# Revit family: RN 91060 Optifitt-Serra-Verlängerung
name_source: partatom
category: Rohrformteile
units: mm (PartAtom-declared; Revit-internal decimal feet)

## family parameters
Arbeitsebenenbasiert = Nein
Beim Laden mit Abzugskörper schneiden = Nein
Bemaßung runder Anschluss = Durchmesser verwenden
Gemeinsam genutzt = Nein
Immer vertikal = Ja
Teiletyp = Nicht definiert

## types (13) — shared parameters
1.010.00.2 Blattnummer der Richtlinie = 29
1.010.00.3 Ausgabedatum (Monat) der Richtlinie = 201308
1.010.00.4 Herstellername = R. Nussbaum AG
1.010.00.5 Revisionsdatum der Datei = 20190521
1.010.00.6 Webadresse des Herstellers = http://www.nussbaum.ch
1.100.00.4 Produktbezeichnung = Versorgung
1.110.00.2 Index = 3
1.110.00.4 Produktbezeichnung = Optifitt-Serra
1.960/3L.00.8 Link (URL) = https://www.nussbaum.ch
29.700.00.4 Produktname = Optifitt-Serra-Verlängerung
29.700.00.5 Produktkennung = 2
29.700.00.6 Querschnittsform = 1
29.700.00.7 Nennweitensystem = DN
29.700.00.8 Nenndrucksystem = PN
29.710.02.4 Nenndruck = 16
29.710.02.5 max. zul. Überdruck [hPa] = 1600
29.710.02.7 max. zul. Dauer-Betriebsdruck [hPa] = 1600
29.710.02.9 max. zul. Dauer-Betriebstemperatur [°C] = 90
Connector Visibility = Nein
EnclosingSpace Visibility = Nein
R. Nussbaum AG 91060.51 de Visibility = Nein
R. Nussbaum AG 91060.52 de Visibility = Nein
R. Nussbaum AG 91060.68 de Visibility = Nein
R. Nussbaum AG 91060.69 de Visibility = Nein
R. Nussbaum AG 91060.71 de Visibility = Nein
R. Nussbaum AG 91060.72 de Visibility = Nein
R. Nussbaum AG 91060.74 de Visibility = Nein

## per-type parameters (varying)
- DN=2: 1.800.00.3 TGA-Nummer=01900300000000000000000000000000000000000000000020000000000000000049; 1.800.00.4 Kommentarfeld=91060.70, Optifitt-Serra-Verlängerung, DN=15, L=100; 1.810.00.3 Hersteller-Bestellnummer=91060.7; 1.810.00.4 DATANORM-Nummer=91060.7; 1.810.00.6 GTIN-Nummer=7612945036476; 29.710.02.10 Formstück-Gewicht [kg]=0.271; 29.710.02.3 Benennung=Optifitt-Serra-Verlängerung, DN=15, L=100; CONNECTOR0_DIAMETER_dX_0r=15 mm; CONNECTOR0_dX_01=11 mm; CONNECTOR0_ref_dX=11 mm; CONNECTOR1_DIAMETER_dX_0r=15 mm; CONNECTOR1_dX_00=98 mm; CONNECTOR1_dX_01=111 mm; CONNECTOR1_ref_dX=98 mm; Hersteller=R. Nussbaum AG; Modell=91060.7; R. Nussbaum AG 91060.53 de Visibility=Nein; R. Nussbaum AG 91060.54 de Visibility=Nein; R. Nussbaum AG 91060.55 de Visibility=Nein; R. Nussbaum AG 91060.56 de Visibility=Nein; R. Nussbaum AG 91060.62 de Visibility=Nein; R. Nussbaum AG 91060.63 de Visibility=Nein; R. Nussbaum AG 91060.64 de Visibility=Nein; R. Nussbaum AG 91060.65 de Visibility=Nein; R. Nussbaum AG 91060.66 de Visibility=Nein; R. Nussbaum AG 91060.67 de Visibility=Nein; R. Nussbaum AG 91060.70 de Visibility=Ja; R. Nussbaum AG 91060.73 de Visibility=Nein; R. Nussbaum AG 91060.75 de Visibility=Nein; Typenkommentare=Optifitt-Serra-Verlängerung  DN=15; URL=https://www.nussbaum.ch
- DN=1: 1.800.00.3 TGA-Nummer=01900300000000000000000000000000000000000000000020000000000000000045; 1.800.00.4 Kommentarfeld=91060.75, Optifitt-Serra-Verlängerung, DN=20, L=40; 1.810.00.3 Hersteller-Bestellnummer=91060.75; 1.810.00.4 DATANORM-Nummer=91060.75; 1.810.00.5 StLB-Nummer=214.413; 1.810.00.6 GTIN-Nummer=7612945036520; 29.710.02.10 Formstück-Gewicht [kg]=0.125; 29.710.02.3 Benennung=Optifitt-Serra-Verlängerung, DN=20, L=40; CONNECTOR0_DIAMETER_dX_0r=20 mm; CONNECTOR0_dX_01=12 mm  [stored 0.0393701 ft]; CONNECTOR0_ref_dX=12 mm  [stored 0.0393701 ft]; CONNECTOR1_DIAMETER_dX_0r=20 mm; CONNECTOR1_dX_00=37 mm; CONNECTOR1_dX_01=52 mm; CONNECTOR1_ref_dX=37 mm; Hersteller=R. Nussbaum AG; Modell=91060.75; R. Nussbaum AG 91060.53 de Visibility=Nein; R. Nussbaum AG 91060.54 de Visibility=Nein; R. Nussbaum AG 91060.55 de Visibility=Nein; R. Nussbaum AG 91060.56 de Visibility=Nein; R. Nussbaum AG 91060.62 de Visibility=Nein; R. Nussbaum AG 91060.63 de Visibility=Nein; R. Nussbaum AG 91060.64 de Visibility=Nein; R. Nussbaum AG 91060.65 de Visibility=Nein; R. Nussbaum AG 91060.66 de Visibility=Nein; R. Nussbaum AG 91060.67 de Visibility=Nein; R. Nussbaum AG 91060.70 de Visibility=Nein; R. Nussbaum AG 91060.73 de Visibility=Nein; R. Nussbaum AG 91060.75 de Visibility=Ja; Typenkommentare=Optifitt-Serra-Verlängerung  DN=20; URL=https://www.nussbaum.ch
- DN=20: 1.800.00.3 TGA-Nummer=01900300000000000000000000000000000000000000000020000000000000000043; 1.800.00.4 Kommentarfeld=91060.73, Optifitt-Serra-Verlängerung, DN=20, L=25; 1.810.00.3 Hersteller-Bestellnummer=91060.73; 1.810.00.4 DATANORM-Nummer=91060.73; 1.810.00.6 GTIN-Nummer=7612945036506; 29.710.02.10 Formstück-Gewicht [kg]=0.094; 29.710.02.3 Benennung=Optifitt-Serra-Verlängerung, DN=20, L=25; CONNECTOR0_DIAMETER_dX_0r=20 mm; CONNECTOR0_dX_01=12 mm  [stored 0.0393701 ft]; CONNECTOR0_ref_dX=12 mm  [stored 0.0393701 ft]; CONNECTOR1_DIAMETER_dX_0r=20 mm; CONNECTOR1_dX_00=22 mm; CONNECTOR1_dX_01=37 mm; CONNECTOR1_ref_dX=22 mm; R. Nussbaum AG 91060.53 de Visibility=Nein; R. Nussbaum AG 91060.54 de Visibility=Nein; R. Nussbaum AG 91060.55 de Visibility=Nein; R. Nussbaum AG 91060.56 de Visibility=Nein; R. Nussbaum AG 91060.62 de Visibility=Nein; R. Nussbaum AG 91060.63 de Visibility=Nein; R. Nussbaum AG 91060.64 de Visibility=Nein; R. Nussbaum AG 91060.65 de Visibility=Nein; R. Nussbaum AG 91060.66 de Visibility=Nein; R. Nussbaum AG 91060.67 de Visibility=Nein; R. Nussbaum AG 91060.70 de Visibility=Nein; R. Nussbaum AG 91060.73 de Visibility=Ja; R. Nussbaum AG 91060.75 de Visibility=Nein
- DN=15: 1.800.00.3 TGA-Nummer=01900300000000000000000000000000000000000000000020000000000000000038; 1.800.00.4 Kommentarfeld=91060.67, Optifitt-Serra-Verlängerung, DN=15, L=50; 1.810.00.3 Hersteller-Bestellnummer=91060.67; 1.810.00.4 DATANORM-Nummer=91060.67; 1.810.00.6 GTIN-Nummer=7612945036445; 29.710.02.10 Formstück-Gewicht [kg]=0.135; 29.710.02.3 Benennung=Optifitt-Serra-Verlängerung, DN=15, L=50; CONNECTOR0_DIAMETER_dX_0r=15 mm; CONNECTOR0_dX_01=11 mm; CONNECTOR0_ref_dX=11 mm; CONNECTOR1_DIAMETER_dX_0r=15 mm; CONNECTOR1_dX_00=48 mm; CONNECTOR1_dX_01=61 mm; CONNECTOR1_ref_dX=48 mm; R. Nussbaum AG 91060.53 de Visibility=Nein; R. Nussbaum AG 91060.54 de Visibility=Nein; R. Nussbaum AG 91060.55 de Visibility=Nein; R. Nussbaum AG 91060.56 de Visibility=Nein; R. Nussbaum AG 91060.62 de Visibility=Nein; R. Nussbaum AG 91060.63 de Visibility=Nein; R. Nussbaum AG 91060.64 de Visibility=Nein; R. Nussbaum AG 91060.65 de Visibility=Nein; R. Nussbaum AG 91060.66 de Visibility=Nein; R. Nussbaum AG 91060.67 de Visibility=Ja; R. Nussbaum AG 91060.70 de Visibility=Nein; R. Nussbaum AG 91060.73 de Visibility=Nein; R. Nussbaum AG 91060.75 de Visibility=Nein
- DN=11: 1.800.00.3 TGA-Nummer=01900300000000000000000000000000000000000000000020000000000000000037; 1.800.00.4 Kommentarfeld=91060.66, Optifitt-Serra-Verlängerung, DN=15, L=40; 1.810.00.3 Hersteller-Bestellnummer=91060.66; 1.810.00.4 DATANORM-Nummer=91060.66; 1.810.00.5 StLB-Nummer=214.412; 1.810.00.6 GTIN-Nummer=7612945036438; 29.710.02.10 Formstück-Gewicht [kg]=0.107; 29.710.02.3 Benennung=Optifitt-Serra-Verlängerung, DN=15, L=40; CONNECTOR0_DIAMETER_dX_0r=15 mm; CONNECTOR0_dX_01=11 mm; CONNECTOR0_ref_dX=11 mm; CONNECTOR1_DIAMETER_dX_0r=15 mm; CONNECTOR1_dX_00=38 mm; CONNECTOR1_dX_01=51 mm; CONNECTOR1_ref_dX=38 mm; Hersteller=R. Nussbaum AG; Modell=91060.66; R. Nussbaum AG 91060.53 de Visibility=Nein; R. Nussbaum AG 91060.54 de Visibility=Nein; R. Nussbaum AG 91060.55 de Visibility=Nein; R. Nussbaum AG 91060.56 de Visibility=Nein; R. Nussbaum AG 91060.62 de Visibility=Nein; R. Nussbaum AG 91060.63 de Visibility=Nein; R. Nussbaum AG 91060.64 de Visibility=Nein; R. Nussbaum AG 91060.65 de Visibility=Nein; R. Nussbaum AG 91060.66 de Visibility=Ja; R. Nussbaum AG 91060.67 de Visibility=Nein; R. Nussbaum AG 91060.70 de Visibility=Nein; R. Nussbaum AG 91060.73 de Visibility=Nein; R. Nussbaum AG 91060.75 de Visibility=Nein; Typenkommentare=Optifitt-Serra-Verlängerung  DN=15; URL=https://www.nussbaum.ch
- DN=9: 1.800.00.3 TGA-Nummer=01900300000000000000000000000000000000000000000020000000000000000036; 1.800.00.4 Kommentarfeld=91060.65, Optifitt-Serra-Verlängerung, DN=15, L=30; 1.810.00.3 Hersteller-Bestellnummer=91060.65; 1.810.00.4 DATANORM-Nummer=91060.65; 1.810.00.6 GTIN-Nummer=7612945036421; 29.710.02.10 Formstück-Gewicht [kg]=0.088; 29.710.02.3 Benennung=Optifitt-Serra-Verlängerung, DN=15, L=30; CONNECTOR0_DIAMETER_dX_0r=15 mm; CONNECTOR0_dX_01=11 mm; CONNECTOR0_ref_dX=11 mm; CONNECTOR1_DIAMETER_dX_0r=15 mm; CONNECTOR1_dX_00=28 mm; CONNECTOR1_dX_01=41 mm; CONNECTOR1_ref_dX=28 mm; Hersteller=R. Nussbaum AG; Modell=91060.65; R. Nussbaum AG 91060.53 de Visibility=Nein; R. Nussbaum AG 91060.54 de Visibility=Nein; R. Nussbaum AG 91060.55 de Visibility=Nein; R. Nussbaum AG 91060.56 de Visibility=Nein; R. Nussbaum AG 91060.62 de Visibility=Nein; R. Nussbaum AG 91060.63 de Visibility=Nein; R. Nussbaum AG 91060.64 de Visibility=Nein; R. Nussbaum AG 91060.65 de Visibility=Ja; R. Nussbaum AG 91060.66 de Visibility=Nein; R. Nussbaum AG 91060.67 de Visibility=Nein; R. Nussbaum AG 91060.70 de Visibility=Nein; R. Nussbaum AG 91060.73 de Visibility=Nein; R. Nussbaum AG 91060.75 de Visibility=Nein; Typenkommentare=Optifitt-Serra-Verlängerung  DN=15; URL=https://www.nussbaum.ch
- DN=8: 1.800.00.3 TGA-Nummer=01900300000000000000000000000000000000000000000020000000000000000035; 1.800.00.4 Kommentarfeld=91060.64, Optifitt-Serra-Verlängerung, DN=15, L=25; 1.810.00.3 Hersteller-Bestellnummer=91060.64; 1.810.00.4 DATANORM-Nummer=91060.64; 1.810.00.6 GTIN-Nummer=7612945036414; 29.710.02.10 Formstück-Gewicht [kg]=0.075; 29.710.02.3 Benennung=Optifitt-Serra-Verlängerung, DN=15, L=25; CONNECTOR0_DIAMETER_dX_0r=15 mm; CONNECTOR0_dX_01=11 mm; CONNECTOR0_ref_dX=11 mm; CONNECTOR1_DIAMETER_dX_0r=15 mm; CONNECTOR1_dX_00=23 mm; CONNECTOR1_dX_01=36 mm; CONNECTOR1_ref_dX=23 mm; Hersteller=R. Nussbaum AG; Modell=91060.64; R. Nussbaum AG 91060.53 de Visibility=Nein; R. Nussbaum AG 91060.54 de Visibility=Nein; R. Nussbaum AG 91060.55 de Visibility=Nein; R. Nussbaum AG 91060.56 de Visibility=Nein; R. Nussbaum AG 91060.62 de Visibility=Nein; R. Nussbaum AG 91060.63 de Visibility=Nein; R. Nussbaum AG 91060.64 de Visibility=Ja; R. Nussbaum AG 91060.65 de Visibility=Nein; R. Nussbaum AG 91060.66 de Visibility=Nein; R. Nussbaum AG 91060.67 de Visibility=Nein; R. Nussbaum AG 91060.70 de Visibility=Nein; R. Nussbaum AG 91060.73 de Visibility=Nein; R. Nussbaum AG 91060.75 de Visibility=Nein; Typenkommentare=Optifitt-Serra-Verlängerung  DN=15; URL=https://www.nussbaum.ch
- DN=7: 1.800.00.3 TGA-Nummer=01900300000000000000000000000000000000000000000020000000000000000034; 1.800.00.4 Kommentarfeld=91060.63, Optifitt-Serra-Verlängerung, DN=15, L=20; 1.810.00.3 Hersteller-Bestellnummer=91060.63; 1.810.00.4 DATANORM-Nummer=91060.63; 1.810.00.6 GTIN-Nummer=7612945036407; 29.710.02.10 Formstück-Gewicht [kg]=0.067; 29.710.02.3 Benennung=Optifitt-Serra-Verlängerung, DN=15, L=20; CONNECTOR0_DIAMETER_dX_0r=15 mm; CONNECTOR0_dX_01=11 mm; CONNECTOR0_ref_dX=11 mm; CONNECTOR1_DIAMETER_dX_0r=15 mm; CONNECTOR1_dX_00=18 mm; CONNECTOR1_dX_01=31 mm; CONNECTOR1_ref_dX=18 mm; Hersteller=R. Nussbaum AG; Modell=91060.63; R. Nussbaum AG 91060.53 de Visibility=Nein; R. Nussbaum AG 91060.54 de Visibility=Nein; R. Nussbaum AG 91060.55 de Visibility=Nein; R. Nussbaum AG 91060.56 de Visibility=Nein; R. Nussbaum AG 91060.62 de Visibility=Nein; R. Nussbaum AG 91060.63 de Visibility=Ja; R. Nussbaum AG 91060.64 de Visibility=Nein; R. Nussbaum AG 91060.65 de Visibility=Nein; R. Nussbaum AG 91060.66 de Visibility=Nein; R. Nussbaum AG 91060.67 de Visibility=Nein; R. Nussbaum AG 91060.70 de Visibility=Nein; R. Nussbaum AG 91060.73 de Visibility=Nein; R. Nussbaum AG 91060.75 de Visibility=Nein; Typenkommentare=Optifitt-Serra-Verlängerung  DN=15; URL=https://www.nussbaum.ch
- DN=3: 1.800.00.3 TGA-Nummer=01900300000000000000000000000000000000000000000020000000000000000033; 1.800.00.4 Kommentarfeld=91060.62, Optifitt-Serra-Verlängerung, DN=15, L=15; 1.810.00.3 Hersteller-Bestellnummer=91060.62; 1.810.00.4 DATANORM-Nummer=91060.62; 1.810.00.6 GTIN-Nummer=7612945036391; 29.710.02.10 Formstück-Gewicht [kg]=0.05; 29.710.02.3 Benennung=Optifitt-Serra-Verlängerung, DN=15, L=15; CONNECTOR0_DIAMETER_dX_0r=15 mm; CONNECTOR0_dX_01=11 mm; CONNECTOR0_ref_dX=11 mm; CONNECTOR1_DIAMETER_dX_0r=15 mm; CONNECTOR1_dX_00=13 mm; CONNECTOR1_dX_01=26 mm; CONNECTOR1_ref_dX=13 mm; Hersteller=R. Nussbaum AG; Modell=91060.62; R. Nussbaum AG 91060.53 de Visibility=Nein; R. Nussbaum AG 91060.54 de Visibility=Nein; R. Nussbaum AG 91060.55 de Visibility=Nein; R. Nussbaum AG 91060.56 de Visibility=Nein; R. Nussbaum AG 91060.62 de Visibility=Ja; R. Nussbaum AG 91060.63 de Visibility=Nein; R. Nussbaum AG 91060.64 de Visibility=Nein; R. Nussbaum AG 91060.65 de Visibility=Nein; R. Nussbaum AG 91060.66 de Visibility=Nein; R. Nussbaum AG 91060.67 de Visibility=Nein; R. Nussbaum AG 91060.70 de Visibility=Nein; R. Nussbaum AG 91060.73 de Visibility=Nein; R. Nussbaum AG 91060.75 de Visibility=Nein; Typenkommentare=Optifitt-Serra-Verlängerung  DN=15; URL=https://www.nussbaum.ch
- DN=10: 1.800.00.3 TGA-Nummer=01900300000000000000000000000000000000000000000020000000000000000032; 1.800.00.4 Kommentarfeld=91060.56, Optifitt-Serra-Verlängerung, DN=10, L=40; 1.810.00.3 Hersteller-Bestellnummer=91060.56; 1.810.00.4 DATANORM-Nummer=91060.56; 1.810.00.5 StLB-Nummer=214.411; 1.810.00.6 GTIN-Nummer=7612945036384; 29.710.02.10 Formstück-Gewicht [kg]=0.075; 29.710.02.3 Benennung=Optifitt-Serra-Verlängerung, DN=10, L=40; CONNECTOR0_DIAMETER_dX_0r=10 mm  [stored 0.0328084 ft]; CONNECTOR0_dX_01=10 mm  [stored 0.0328084 ft]; CONNECTOR0_ref_dX=10 mm  [stored 0.0328084 ft]; CONNECTOR1_DIAMETER_dX_0r=10 mm  [stored 0.0328084 ft]; CONNECTOR1_dX_00=40 mm; CONNECTOR1_dX_01=50 mm; CONNECTOR1_ref_dX=40 mm; Hersteller=R. Nussbaum AG; Modell=91060.56; R. Nussbaum AG 91060.53 de Visibility=Nein; R. Nussbaum AG 91060.54 de Visibility=Nein; R. Nussbaum AG 91060.55 de Visibility=Nein; R. Nussbaum AG 91060.56 de Visibility=Ja; R. Nussbaum AG 91060.62 de Visibility=Nein; R. Nussbaum AG 91060.63 de Visibility=Nein; R. Nussbaum AG 91060.64 de Visibility=Nein; R. Nussbaum AG 91060.65 de Visibility=Nein; R. Nussbaum AG 91060.66 de Visibility=Nein; R. Nussbaum AG 91060.67 de Visibility=Nein; R. Nussbaum AG 91060.70 de Visibility=Nein; R. Nussbaum AG 91060.73 de Visibility=Nein; R. Nussbaum AG 91060.75 de Visibility=Nein; Typenkommentare=Optifitt-Serra-Verlängerung  DN=10; URL=https://www.nussbaum.ch
- DN=6: 1.800.00.3 TGA-Nummer=01900300000000000000000000000000000000000000000020000000000000000031; 1.800.00.4 Kommentarfeld=91060.55, Optifitt-Serra-Verlängerung, DN=10, L=30; 1.810.00.3 Hersteller-Bestellnummer=91060.55; 1.810.00.4 DATANORM-Nummer=91060.55; 1.810.00.6 GTIN-Nummer=7612945036377; 29.710.02.10 Formstück-Gewicht [kg]=0.06; 29.710.02.3 Benennung=Optifitt-Serra-Verlängerung, DN=10, L=30; CONNECTOR0_DIAMETER_dX_0r=10 mm  [stored 0.0328084 ft]; CONNECTOR0_dX_01=10 mm  [stored 0.0328084 ft]; CONNECTOR0_ref_dX=10 mm  [stored 0.0328084 ft]; CONNECTOR1_DIAMETER_dX_0r=10 mm  [stored 0.0328084 ft]; CONNECTOR1_dX_00=30 mm; CONNECTOR1_dX_01=40 mm; CONNECTOR1_ref_dX=30 mm; Hersteller=R. Nussbaum AG; Modell=91060.55; R. Nussbaum AG 91060.53 de Visibility=Nein; R. Nussbaum AG 91060.54 de Visibility=Nein; R. Nussbaum AG 91060.55 de Visibility=Ja; R. Nussbaum AG 91060.56 de Visibility=Nein; R. Nussbaum AG 91060.62 de Visibility=Nein; R. Nussbaum AG 91060.63 de Visibility=Nein; R. Nussbaum AG 91060.64 de Visibility=Nein; R. Nussbaum AG 91060.65 de Visibility=Nein; R. Nussbaum AG 91060.66 de Visibility=Nein; R. Nussbaum AG 91060.67 de Visibility=Nein; R. Nussbaum AG 91060.70 de Visibility=Nein; R. Nussbaum AG 91060.73 de Visibility=Nein; R. Nussbaum AG 91060.75 de Visibility=Nein; Typenkommentare=Optifitt-Serra-Verlängerung  DN=10; URL=https://www.nussbaum.ch
- DN=5: 1.800.00.3 TGA-Nummer=01900300000000000000000000000000000000000000000020000000000000000030; 1.800.00.4 Kommentarfeld=91060.54, Optifitt-Serra-Verlängerung, DN=10, L=25; 1.810.00.3 Hersteller-Bestellnummer=91060.54; 1.810.00.4 DATANORM-Nummer=91060.54; 1.810.00.6 GTIN-Nummer=7612945036360; 29.710.02.10 Formstück-Gewicht [kg]=0.052; 29.710.02.3 Benennung=Optifitt-Serra-Verlängerung, DN=10, L=25; CONNECTOR0_DIAMETER_dX_0r=10 mm  [stored 0.0328084 ft]; CONNECTOR0_dX_01=10 mm  [stored 0.0328084 ft]; CONNECTOR0_ref_dX=10 mm  [stored 0.0328084 ft]; CONNECTOR1_DIAMETER_dX_0r=10 mm  [stored 0.0328084 ft]; CONNECTOR1_dX_00=25 mm  [stored 0.082021 ft]; CONNECTOR1_dX_01=35 mm; CONNECTOR1_ref_dX=25 mm  [stored 0.082021 ft]; Hersteller=R. Nussbaum AG; Modell=91060.54; R. Nussbaum AG 91060.53 de Visibility=Nein; R. Nussbaum AG 91060.54 de Visibility=Ja; R. Nussbaum AG 91060.55 de Visibility=Nein; R. Nussbaum AG 91060.56 de Visibility=Nein; R. Nussbaum AG 91060.62 de Visibility=Nein; R. Nussbaum AG 91060.63 de Visibility=Nein; R. Nussbaum AG 91060.64 de Visibility=Nein; R. Nussbaum AG 91060.65 de Visibility=Nein; R. Nussbaum AG 91060.66 de Visibility=Nein; R. Nussbaum AG 91060.67 de Visibility=Nein; R. Nussbaum AG 91060.70 de Visibility=Nein; R. Nussbaum AG 91060.73 de Visibility=Nein; R. Nussbaum AG 91060.75 de Visibility=Nein; Typenkommentare=Optifitt-Serra-Verlängerung  DN=10; URL=https://www.nussbaum.ch
- DN=4: 1.800.00.3 TGA-Nummer=01900300000000000000000000000000000000000000000020000000000000000029; 1.800.00.4 Kommentarfeld=91060.53, Optifitt-Serra-Verlängerung, DN=10, L=20; 1.810.00.3 Hersteller-Bestellnummer=91060.53; 1.810.00.4 DATANORM-Nummer=91060.53; 1.810.00.6 GTIN-Nummer=7612945036353; 29.710.02.10 Formstück-Gewicht [kg]=0.044; 29.710.02.3 Benennung=Optifitt-Serra-Verlängerung, DN=10, L=20; CONNECTOR0_DIAMETER_dX_0r=10 mm  [stored 0.0328084 ft]; CONNECTOR0_dX_01=10 mm  [stored 0.0328084 ft]; CONNECTOR0_ref_dX=10 mm  [stored 0.0328084 ft]; CONNECTOR1_DIAMETER_dX_0r=10 mm  [stored 0.0328084 ft]; CONNECTOR1_dX_00=20 mm; CONNECTOR1_dX_01=30 mm; CONNECTOR1_ref_dX=20 mm; Hersteller=R. Nussbaum AG; Modell=91060.53; R. Nussbaum AG 91060.53 de Visibility=Ja; R. Nussbaum AG 91060.54 de Visibility=Nein; R. Nussbaum AG 91060.55 de Visibility=Nein; R. Nussbaum AG 91060.56 de Visibility=Nein; R. Nussbaum AG 91060.62 de Visibility=Nein; R. Nussbaum AG 91060.63 de Visibility=Nein; R. Nussbaum AG 91060.64 de Visibility=Nein; R. Nussbaum AG 91060.65 de Visibility=Nein; R. Nussbaum AG 91060.66 de Visibility=Nein; R. Nussbaum AG 91060.67 de Visibility=Nein; R. Nussbaum AG 91060.70 de Visibility=Nein; R. Nussbaum AG 91060.73 de Visibility=Nein; R. Nussbaum AG 91060.75 de Visibility=Nein; Typenkommentare=Optifitt-Serra-Verlängerung  DN=10; URL=https://www.nussbaum.ch

note: [stored X ft] marks values corroborated as IEEE doubles in the binary element streams (Revit-internal decimal feet)

## geometry (parser evidence)
native form markers: Sweep x3
no freeform markers — native parametric forms only
